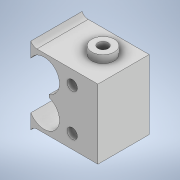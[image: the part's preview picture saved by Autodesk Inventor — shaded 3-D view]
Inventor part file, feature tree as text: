
AUTODESK INVENTOR PART (.ipt)
format: ipt  version: 2022 (Build 260153000, 153)  size: 327,680 bytes
history: native  units: mm
features: reference x16, other x13, extrude x11, sketch x9, projected_geometry x8
ambient origin geometry x8: Origin, YZ Plane, XZ Plane, XY Plane, X Axis, Y Axis, Z Axis, Center Point
bodies: Solid1 (feature_tree)
feature tree (57):
  extrude  "Extrusion1"  Depth=6.0mm
  extrude  "Extrusion2"  Depth=10.0mm TaperAngle=0.0deg
  extrude  "Extrusion3"  TaperAngle=0.0deg  [1 undecoded]
  sketch  "Sketch4"  dims[d9=1.5mm d10=0.0mm d11=1.0mm d12=0.0mm]
  extrude  "Extrusion4"  Depth=1.0mm TaperAngle=0.0deg
  extrude  "Extrusion5"  TaperAngle=0.0deg  [1 undecoded]
  extrude  "Extrusion6"  Depth=10.0mm TaperAngle=0.0deg
  extrude  "Extrusion7"  Depth=10.0mm TaperAngle=0.0deg
  extrude  "Extrusion8"  Depth=10.0mm TaperAngle=0.0deg
  sketch  "Sketch8"  dims[d23=10.0mm d24=0.0mm d25=10.0mm d26=0.0mm]
  extrude  "Extrusion9"  [1 undecoded]
  extrude  "Extrusion10"  [1 undecoded]
  extrude  "Extrusion11"  [1 undecoded]
  sketch  "Sketch1"  dims[d0=6.0mm d1=6.0mm]
  reference  "Reference1"
  reference  "Reference2"
  reference  "Reference3"
  reference  "Reference4"
  reference  "Reference5"
  reference  "Reference6"
  reference  "Reference7"
  reference  "Reference8"
  reference  "Reference9"
  reference  "Reference10"
  reference  "Reference11"
  reference  "Reference12"
  reference  "Reference13"
  reference  "Reference14"
  reference  "Reference15"
  sketch  "Sketch2"  dims[d2=10.0mm d3=0.0mm d4=10.0mm d5=0.0mm]
  projected_geometry  "Projected Loop1"
  sketch  "Sketch3"  dims[d6=2.0mm d7=0.0mm d8=0.0mm]
  projected_geometry  "Projected Loop2"
  reference  "Reference16"
  sketch  "Sketch5"  dims[d13=16.532mm d14=0.0mm d15=0.0mm d16=0.0mm]
  projected_geometry  "Projected Loop3"
  sketch  "Sketch6"  dims[d17=1.5mm d18=10.0mm d19=0.0mm]
  projected_geometry  "Projected Loop4"
  projected_geometry  "Projected Loop5"
  sketch  "Sketch7"  dims[d20=0.5mm d21=10.0mm d22=0.0mm]
  projected_geometry  "Projected Loop6"
  projected_geometry  "Projected Loop7"
  sketch  "Sketch9"
  projected_geometry  "Projected Loop8"
  parser-record x1  (decoder bookkeeping rows leaked as tree rows — omitted from the tree; the rows remain in map.json)
  other  "Przekładnia.iam"
  other  "Spur Gears:2"
  other  "Spur Gear2:1"
  other  "Spur Gears2_MIR1:1"
  other  "Spur Gear22_MIR1:1"
  other  "silnik_2:3"
  other  "silnik_2:1"
  other  "kokool:2"
  other  "<userpath>\Documents\Inventor\NanoSumo\Przekładnia.iam"
  other  "kokool:3"
  other  "Moteur - Engrenage 3_MIR1:1"
  other  "Moteur - Engrenage 3:2"
note: 5 required parameter values undecoded (feature->parameter linkage not recoverable at this tier; creation-order binding heuristic only, values carry confidence <= 0.55)
note: 1 file-system path scrubbed to <path> (originals preserved in map.json)
